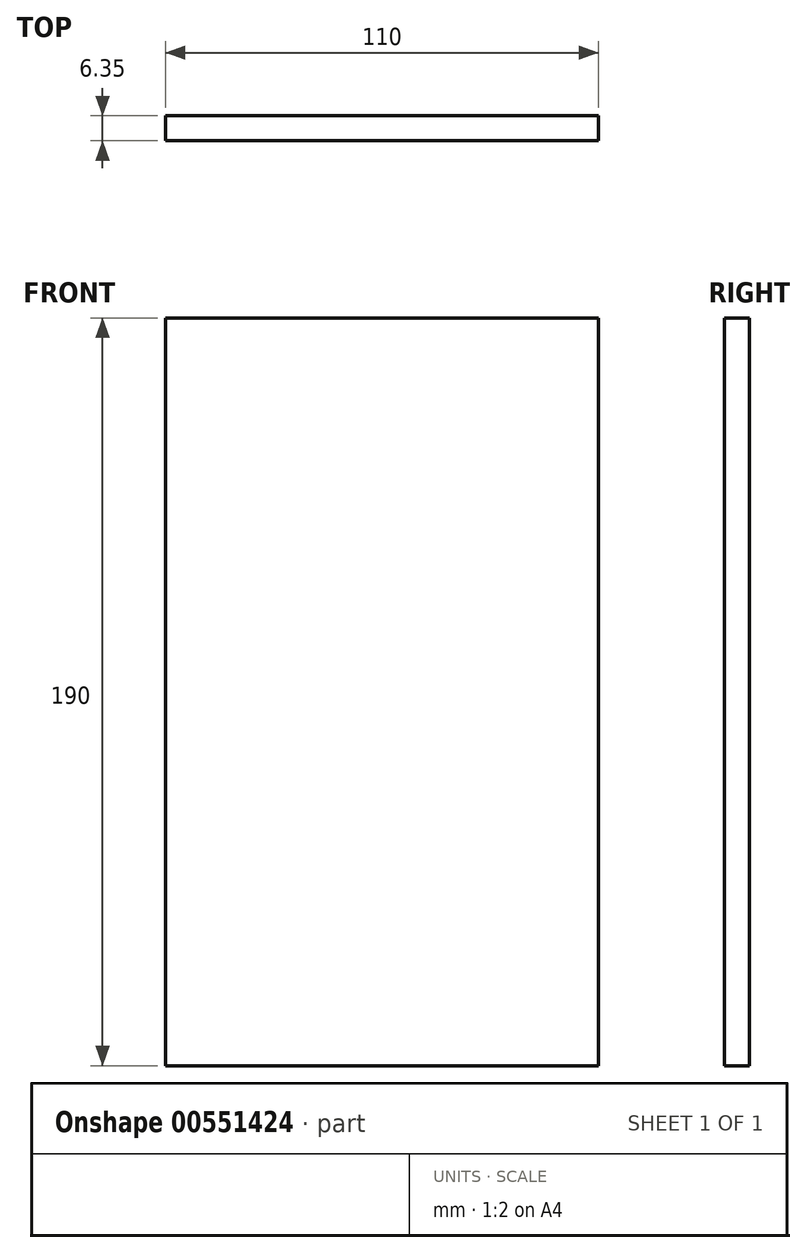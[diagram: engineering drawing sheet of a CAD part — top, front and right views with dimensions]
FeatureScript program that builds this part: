
annotation { "Feature Type Name" : "Feature", "Feature Type Description" : "" }
export const myFeature = defineFeature(function(context is Context, id is Id, definition is map)
    precondition{}
    {
        {
            var Q0;
            Q0=qCreatedBy(makeId("Front.planeOp"),FACE);
            var sketch = newSketch(context, id + "F0", { "sketchPlane" : qUnion([Q0])});
            skLineSegment(sketch, "E0", {"start": v(-48.56, 103.86) * mm, "end": v(-48.56, -86.14) * mm});
            skLineSegment(sketch, "E1", {"start": v(-48.56, -86.14) * mm, "end": v(61.44, -86.14) * mm});
            skLineSegment(sketch, "E2", {"start": v(-48.56, 103.86) * mm, "end": v(62.82, 103.86) * mm});
            skLineSegment(sketch, "E3", {"start": v(61.44, -86.14) * mm, "end": v(61.44, 103.86) * mm});
            skSolve(sketch);
        }
        {
            var Q0;
            {var subQ0=sQuery(id+"F0.wireOp",EDGE,"E0");Q0=makeQuery(id+"F0.imprint","IMPRINT",FACE,{"disambiguationData":[TD([[makeQuery(id+"F0.imprint","IMPRINT",EDGE,{"derivedFrom":subQ0}),1.0]])]});}
            extrude(context, id + "F1", {"entities" : qUnion([Q0]), "depth" : 6.35 * mm, "offsetDistance" : 25.4 * mm});
        }
    });
